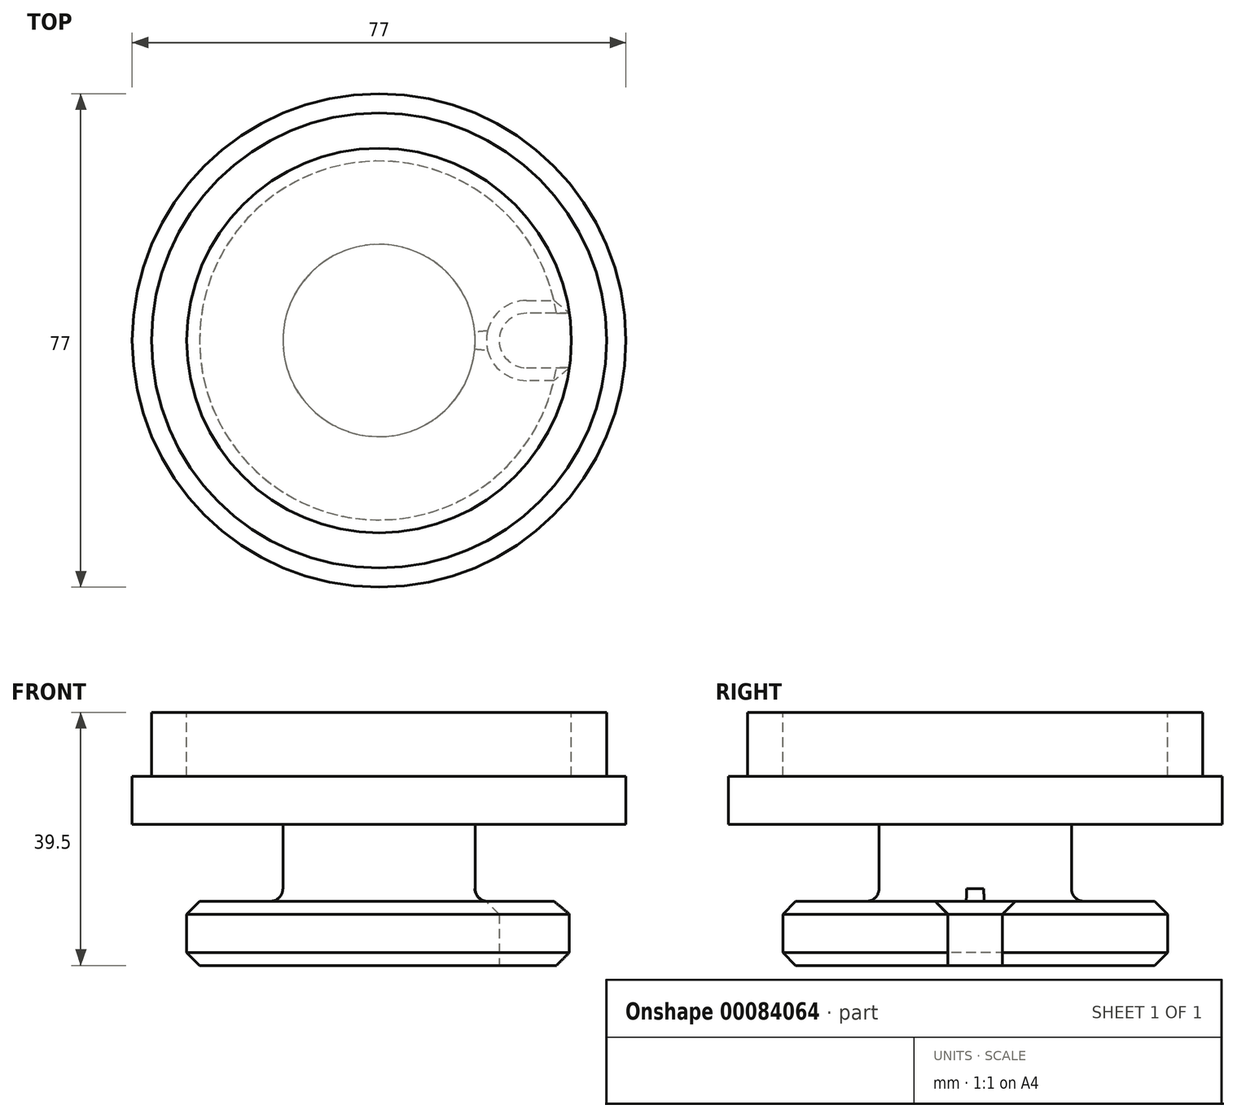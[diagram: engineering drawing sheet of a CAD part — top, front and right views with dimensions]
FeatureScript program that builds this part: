
annotation { "Feature Type Name" : "Feature", "Feature Type Description" : "" }
export const myFeature = defineFeature(function(context is Context, id is Id, definition is map)
    precondition{}
    {
        {
            var Q0;
            Q0=qCreatedBy(makeId("Front.planeOp"),FACE);
            var sketch = newSketch(context, id + "F0", { "sketchPlane" : qUnion([Q0])});
            skLineSegment(sketch, "E0", {"start": v(0, 0) * mm, "end": v(30, 0) * mm});
            skLineSegment(sketch, "E1", {"start": v(30, 0) * mm, "end": v(30, 10) * mm});
            skLineSegment(sketch, "E2", {"start": v(30, 10) * mm, "end": v(15, 10) * mm});
            skLineSegment(sketch, "E3", {"start": v(15, 10) * mm, "end": v(15, 22) * mm});
            skLineSegment(sketch, "E4", {"start": v(15, 22) * mm, "end": v(0, 22) * mm});
            skLineSegment(sketch, "E5", {"start": v(0, 22) * mm, "end": v(0, 0) * mm});
            skLineSegment(sketch, "E6", {"start": v(15, 22) * mm, "end": v(38.5, 22) * mm});
            skLineSegment(sketch, "E7", {"start": v(38.5, 22) * mm, "end": v(38.5, 29.5) * mm});
            skLineSegment(sketch, "E8", {"start": v(38.5, 29.5) * mm, "end": v(35.5, 29.5) * mm});
            skLineSegment(sketch, "E9", {"start": v(35.5, 29.5) * mm, "end": v(35.5, 39.5) * mm});
            skLineSegment(sketch, "E10", {"start": v(0, 37) * mm, "end": v(0, 22) * mm});
            skLineSegment(sketch, "E11", {"start": v(0, 29.5) * mm, "end": v(30, 29.5) * mm});
            skPoint(sketch, "E11.endSnap0", {"position": v(0, 29.5) * mm});
            skLineSegment(sketch, "E12", {"start": v(30, 29.5) * mm, "end": v(30, 39.5) * mm});
            skLineSegment(sketch, "E13", {"start": v(30, 39.5) * mm, "end": v(35.5, 39.5) * mm});
            skSolve(sketch);
        }
        {
            var Q0;
            Q0=makeQuery(id+"F0.imprint","IMPRINT",FACE,{"disambiguationData":[TD([[makeQuery(id+"F0.imprint","IMPRINT",EDGE,{"derivedFrom":sQuery(id+"F0.wireOp",EDGE,"E0")}),1.0]])]});
            var Q1;
            Q1=sQuery(id+"F0.wireOp",EDGE,"E5");
            revolve(context, id + "F1", {"entities" : qUnion([Q0]), "axis" : qUnion([Q1]), "revolveType" : RevolveType.FULL});
        }
        {
            var Q0;
            Q0=qCreatedBy(makeId("Top.planeOp"),FACE);
            var sketch = newSketch(context, id + "F2", { "sketchPlane" : qUnion([Q0])});
            skCircle(sketch, "E14", {"center": v(23, 0) * mm, "radius": 4.25 * mm});
            skLineSegment(sketch, "E15", {"start": v(23, -4.25) * mm, "end": v(43, -4.25) * mm});
            skLineSegment(sketch, "E16", {"start": v(43, -4.25) * mm, "end": v(43, 4.25) * mm});
            skLineSegment(sketch, "E17", {"start": v(43, 4.25) * mm, "end": v(23, 4.25) * mm});
            skSolve(sketch);
        }
        {
            var Q0;
            {var subQ0=sQuery(id+"F2.wireOp",EDGE,"E14");var subQ1=makeQuery(id+"F2.imprint","INTERSECT",VERTEX,{"derivedFrom":[subQ0,sQuery(id+"F2.wireOp",EDGE,"E15")]});Q0=makeQuery(id+"F2.imprint","IMPRINT",FACE,{"disambiguationData":[TD([[makeQuery(id+"F2.imprint","IMPRINT",EDGE,{"disambiguationData":[TD([[subQ1,1.0]])],"derivedFrom":subQ0}),1.0]])]});}
            var Q1;
            {var subQ0=sQuery(id+"F2.wireOp",EDGE,"E15");Q1=makeQuery(id+"F2.imprint","IMPRINT",FACE,{"disambiguationData":[TD([[makeQuery(id+"F2.imprint","IMPRINT",EDGE,{"derivedFrom":subQ0}),1.0]])]});}
            var Q2;
            Q2=sQuery(id+"F2.wireOp",EDGE,"E16");
            var Q3;
            Q3=sQuery(id+"F2.wireOp",EDGE,"E15");
            var Q4;
            Q4=sQuery(id+"F2.wireOp",EDGE,"E14");
            var Q5;
            Q5=sQuery(id+"F2.wireOp",EDGE,"E17");
            extrude(context, id + "F3", {"entities" : qUnion([Q0, Q1]), "operationType" : NewBodyOperationType.REMOVE, "surfaceEntities" : qUnion([Q2, Q3, Q4, Q5]), "depth" : 25 * mm});
        }
        {
            var Q0;
            Q0=makeQuery(id+"F1.opRevolve","SWEPT_EDGE",EDGE,{"disambiguationData":[OSD([sQuery(id+"F0.wireOp",EDGE,"E0"),sQuery(id+"F0.wireOp",EDGE,"E1")])]});
            var Q1;
            Q1=makeQuery(id+"F3.boolean.opBoolean","COPY",EDGE,{"derivedFrom":makeQuery(id+"F3.opExtrude","CAP_EDGE",EDGE,{"disambiguationData":[OSD([sQuery(id+"F2.wireOp",EDGE,"E15")])],"isStart":true})});
            var Q2;
            Q2=makeQuery(id+"F3.boolean.opBoolean","COPY",EDGE,{"derivedFrom":makeQuery(id+"F3.opExtrude","CAP_EDGE",EDGE,{"disambiguationData":[OSD([sQuery(id+"F2.wireOp",EDGE,"E14")])],"isStart":true})});
            var Q3;
            Q3=makeQuery(id+"F1.opRevolve","SWEPT_EDGE",EDGE,{"disambiguationData":[OSD([sQuery(id+"F0.wireOp",EDGE,"E1"),sQuery(id+"F0.wireOp",EDGE,"E2")])]});
            var Q4;
            Q4=makeQuery(id+"F3.boolean.opBoolean","INTERSECT",EDGE,{"derivedFrom":[makeQuery(id+"F1.opRevolve","SWEPT_FACE",FACE,{"disambiguationData":[OSD([sQuery(id+"F0.wireOp",EDGE,"E2")])]}),makeQuery(id+"F3.opExtrude","SWEPT_FACE",FACE,{"disambiguationData":[OSD([sQuery(id+"F2.wireOp",EDGE,"E14")])]})]});
            chamfer(context, id + "F4", {"entities" : qUnion([Q0, Q1, Q2, Q3, Q4]), "width" : 2 * mm, "tangentPropagation" : true});
        }
        {
            var Q0;
            Q0=makeQuery(id+"F1.opRevolve","SWEPT_EDGE",EDGE,{"disambiguationData":[OSD([sQuery(id+"F0.wireOp",EDGE,"E2"),sQuery(id+"F0.wireOp",EDGE,"E3")])]});
            fillet(context, id + "F5", {"entities" : qUnion([Q0]), "radius" : 2 * mm, "tangentPropagation" : true, "allowEdgeOverflow" : false});
        }
        {
            var Q0;
            Q0=makeQuery(id+"F0.imprint","IMPRINT",FACE,{"disambiguationData":[TD([[makeQuery(id+"F0.imprint","IMPRINT",EDGE,{"derivedFrom":sQuery(id+"F0.wireOp",EDGE,"E4")}),-1.0]])]});
            var Q1;
            Q1=sQuery(id+"F0.wireOp",EDGE,"E5");
            revolve(context, id + "F6", {"operationType" : NewBodyOperationType.ADD, "entities" : qUnion([Q0]), "axis" : qUnion([Q1]), "revolveType" : RevolveType.FULL});
        }
    });
